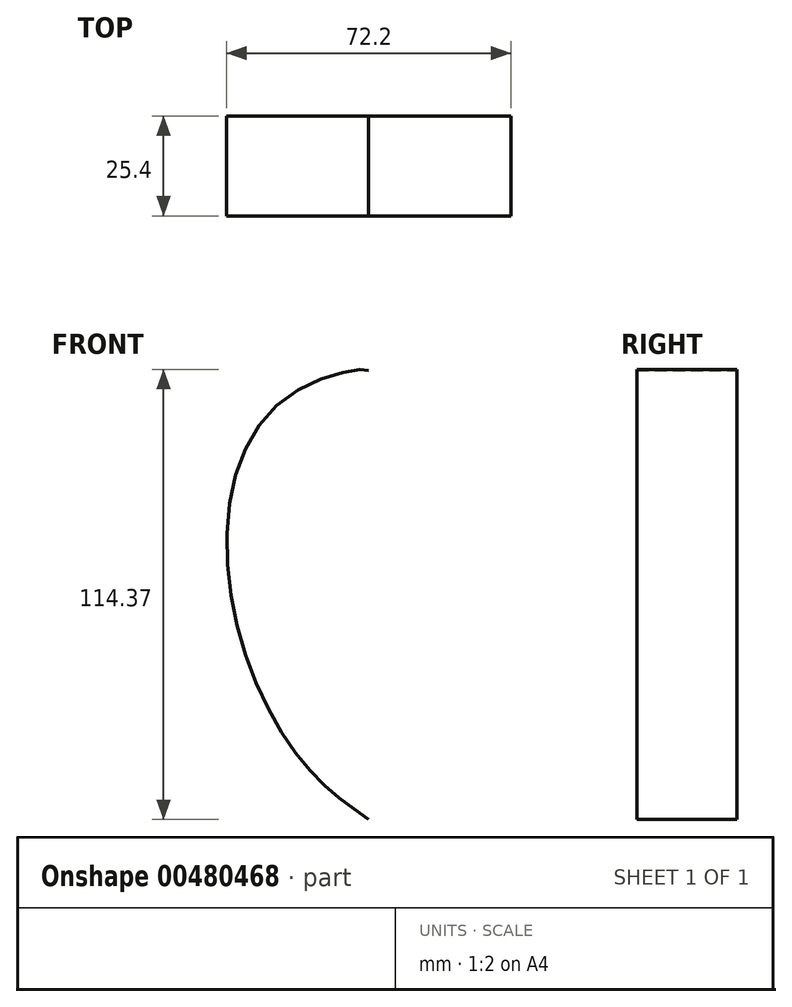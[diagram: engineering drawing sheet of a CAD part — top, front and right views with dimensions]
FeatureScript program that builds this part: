
annotation { "Feature Type Name" : "Feature", "Feature Type Description" : "" }
export const myFeature = defineFeature(function(context is Context, id is Id, definition is map)
    precondition{}
    {
        {
            var Q0;
            Q0=qCreatedBy(makeId("Front.planeOp"),FACE);
            var sketch = newSketch(context, id + "F0", { "sketchPlane" : qUnion([Q0])});
            skFitSpline(sketch, "E0", {"points": [v(0, -39.48) * mm, v(-17.69, -23.78) * mm, v(-35.67, 22.3) * mm, v(-21.94, 67) * mm, v(0, 74.6) * mm, v(0, 73.63) * mm], "startDerivative": vector(-90.46, 62.88) * mm, "endDerivative": vector(-11.22, -27.76) * mm});
            skLineSegment(sketch, "E1", {"start": v(0, -74) * mm, "end": v(0, 74.6) * mm});
            skFitSpline(sketch, "E2.MirrorCS", {"points": [v(0, -39.48) * mm, v(17.69, -23.78) * mm, v(35.67, 22.3) * mm, v(21.94, 67) * mm, v(0, 74.6) * mm, v(0, 73.63) * mm], "startDerivative": vector(90.46, 62.88) * mm, "endDerivative": vector(11.22, -27.76) * mm});
            skLineSegment(sketch, "E3", {"start": v(0, -39.48) * mm, "end": v(-22.35, -55.61) * mm});
            skLineSegment(sketch, "E4", {"start": v(0, -39.48) * mm, "end": v(19.82, -55.61) * mm});
            skSolve(sketch);
        }
        {
            var Q0;
            {var subQ0=sQuery(id+"F0.wireOp",EDGE,"E2.MirrorCS");var subQ1=sQuery(id+"F0.wireOp",EDGE,"E1");var subQ2=sQuery(id+"F0.wireOp",EDGE,"E0");var subQ3=makeQuery(id+"F0.imprint","INTERSECT",VERTEX,{"disambiguationData":[OD(0.0)],"derivedFrom":[subQ2,subQ1,subQ0]});Q0=makeQuery(id+"F0.imprint","IMPRINT",FACE,{"disambiguationData":[TD([[makeQuery(id+"F0.imprint","IMPRINT",EDGE,{"disambiguationData":[TD([[subQ3,-1.0]])],"derivedFrom":subQ2}),-1.0]])]});}
            var Q1;
            Q1 = qSketchRegion(id + "F0", true);
            var Q2;
            {var subQ0=sQuery(id+"F0.wireOp",EDGE,"E2.MirrorCS");var subQ1=sQuery(id+"F0.wireOp",EDGE,"E1");var subQ2=sQuery(id+"F0.wireOp",EDGE,"E0");var subQ3=makeQuery(id+"F0.imprint","INTERSECT",VERTEX,{"disambiguationData":[OD(1.0)],"derivedFrom":[subQ2,subQ1,subQ0]});Q2=makeQuery(id+"F0.imprint","IMPRINT",FACE,{"disambiguationData":[TD([[makeQuery(id+"F0.imprint","IMPRINT",EDGE,{"disambiguationData":[TD([[subQ3,1.0]])],"derivedFrom":subQ2}),1.0]])]});}
            extrude(context, id + "F1", {"entities" : qUnion([Q0, Q1, Q2]), "depth" : 25.4 * mm});
        }
    });
